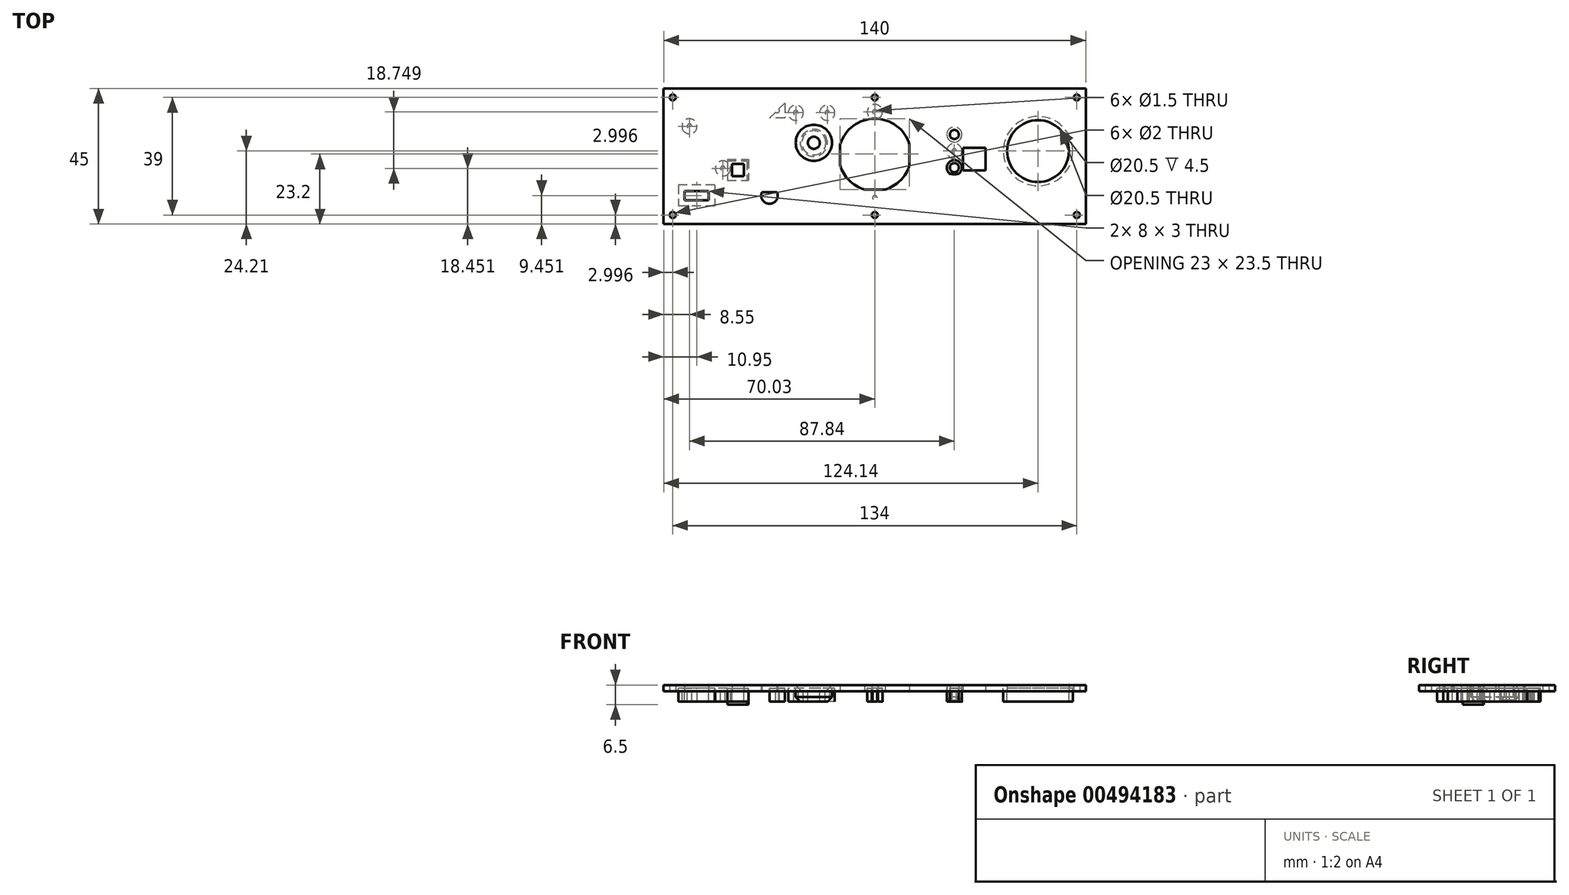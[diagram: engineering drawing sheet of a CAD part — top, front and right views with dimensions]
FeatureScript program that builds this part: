
annotation { "Feature Type Name" : "Feature", "Feature Type Description" : "" }
export const myFeature = defineFeature(function(context is Context, id is Id, definition is map)
    precondition{}
    {
        {
            var Q0;
            Q0=qCreatedBy(makeId("Top.planeOp"),FACE);
            var sketch = newSketch(context, id + "F0", { "sketchPlane" : qUnion([Q0])});
            skLineSegment(sketch, "E0.bottom", {"start": v(12.5, 16.5) * mm, "end": v(1.09, 16.5) * mm});
            skLineSegment(sketch, "E0.top", {"start": v(12.5, -16.5) * mm, "end": v(1.09, -16.5) * mm});
            skLineSegment(sketch, "E0.left", {"start": v(12.5, 16.5) * mm, "end": v(12.5, -16.5) * mm});
            skLineSegment(sketch, "E0.right", {"start": v(-12.5, 16.5) * mm, "end": v(-12.5, -16.5) * mm});
            skPoint(sketch, "E0.middle", {"position": v(0, 0) * mm});
            skCircle(sketch, "E1", {"center": v(0, 0) * mm, "radius": 12 * mm});
            skCircle(sketch, "E2", {"center": v(0, 14.25) * mm, "radius": 0.75 * mm});
            skPoint(sketch, "E2.centerSnap0", {"position": v(0, 16.5) * mm});
            skCircle(sketch, "E3.MirrorC", {"center": v(0, -14.25) * mm, "radius": 0.75 * mm});
            skLineSegment(sketch, "E4.0", {"start": v(9.5, 4.98) * mm, "end": v(9.5, -5.67) * mm, "construction": true});
            skLineSegment(sketch, "E5.bottom", {"start": v(10.77, 1.27) * mm, "end": v(8.23, 1.27) * mm});
            skLineSegment(sketch, "E5.top", {"start": v(10.77, -1.27) * mm, "end": v(8.23, -1.27) * mm});
            skLineSegment(sketch, "E5.left", {"start": v(10.77, 1.27) * mm, "end": v(10.77, -1.27) * mm});
            skLineSegment(sketch, "E5.right", {"start": v(8.23, 1.27) * mm, "end": v(8.23, -1.27) * mm});
            skPoint(sketch, "E5.middle", {"position": v(9.5, 0) * mm});
            skPoint(sketch, "E5.middle.positionSnap0", {"position": v(12.5, 0) * mm});
            skPoint(sketch, "E5.centerSnap0", {"position": v(12.5, 0) * mm});
            skLineSegment(sketch, "E6.MirrorCS", {"start": v(8.23, 1.27) * mm, "end": v(8.23, 3.81) * mm});
            skLineSegment(sketch, "E7.MirrorCS", {"start": v(10.77, 1.27) * mm, "end": v(10.77, 3.81) * mm});
            skLineSegment(sketch, "E8.MirrorCS", {"start": v(10.77, 3.81) * mm, "end": v(8.23, 3.81) * mm});
            skPoint(sketch, "E9.MirrorP", {"position": v(9.5, 2.54) * mm});
            skLineSegment(sketch, "E10.MirrorCS", {"start": v(8.23, -3.81) * mm, "end": v(8.23, -1.27) * mm});
            skLineSegment(sketch, "E11.MirrorCS", {"start": v(10.77, -3.8) * mm, "end": v(10.77, -1.27) * mm});
            skLineSegment(sketch, "E12.MirrorCS", {"start": v(10.77, -3.8) * mm, "end": v(8.23, -3.81) * mm});
            skPoint(sketch, "E13.MirrorP", {"position": v(9.5, -2.54) * mm});
            skLineSegment(sketch, "E14.bottom", {"start": v(-11.5, 11.5) * mm, "end": v(11.5, 11.5) * mm});
            skLineSegment(sketch, "E14.top", {"start": v(-11.5, -11.5) * mm, "end": v(11.5, -11.5) * mm});
            skLineSegment(sketch, "E14.left", {"start": v(-11.5, 11.5) * mm, "end": v(-11.5, -11.5) * mm});
            skLineSegment(sketch, "E14.right", {"start": v(11.5, 11.5) * mm, "end": v(11.5, -11.5) * mm});
            skArc(sketch, "E15", {"start": v(1, 11.96) * mm, "mid": v(0, 16.75) * mm, "end": v(-1, 11.96) * mm});
            skArc(sketch, "E16.MirrorC", {"start": v(1, -11.96) * mm, "mid": v(0, -16.75) * mm, "end": v(-1, -11.96) * mm});
            skLineSegment(sketch, "E17.trimOffspring", {"start": v(-1.09, -16.5) * mm, "end": v(-12.5, -16.5) * mm});
            skLineSegment(sketch, "E18.trimOffspring", {"start": v(-1.09, 16.5) * mm, "end": v(-12.5, 16.5) * mm});
            skSolve(sketch);
        }
        {
            var Q0;
            Q0=qCreatedBy(makeId("Top.planeOp"),FACE);
            var sketch = newSketch(context, id + "F1", { "sketchPlane" : qUnion([Q0])});
            skPoint(sketch, "E19.middle", {"position": v(39.17, 0) * mm});
            skLineSegment(sketch, "E20.bottom", {"start": v(20.93, 1.26) * mm, "end": v(18.4, 1.26) * mm});
            skLineSegment(sketch, "E20.top", {"start": v(20.93, -1.28) * mm, "end": v(18.4, -1.28) * mm});
            skLineSegment(sketch, "E20.left", {"start": v(20.93, 1.26) * mm, "end": v(20.93, -1.28) * mm});
            skLineSegment(sketch, "E20.right", {"start": v(18.4, 1.26) * mm, "end": v(18.4, -1.28) * mm});
            skPoint(sketch, "E20.middle", {"position": v(19.66, 0) * mm});
            skLineSegment(sketch, "E21.MirrorCS", {"start": v(18.4, 1.26) * mm, "end": v(18.4, 3.8) * mm});
            skLineSegment(sketch, "E22.MirrorCS", {"start": v(20.93, 1.26) * mm, "end": v(20.93, 3.8) * mm});
            skLineSegment(sketch, "E23.MirrorCS", {"start": v(20.93, 3.8) * mm, "end": v(18.4, 3.8) * mm});
            skPoint(sketch, "E24.MirrorP", {"position": v(19.66, 2.53) * mm});
            skLineSegment(sketch, "E25.MirrorCS", {"start": v(18.4, -3.82) * mm, "end": v(18.4, -1.28) * mm});
            skLineSegment(sketch, "E26.MirrorCS", {"start": v(20.93, -3.82) * mm, "end": v(20.93, -1.28) * mm});
            skLineSegment(sketch, "E27.MirrorCS", {"start": v(20.93, -3.82) * mm, "end": v(18.4, -3.82) * mm});
            skPoint(sketch, "E28.MirrorP", {"position": v(19.66, -2.55) * mm});
            skLineSegment(sketch, "E29", {"start": v(13.21, 0) * mm, "end": v(-19.23, 0) * mm, "construction": true});
            skLineSegment(sketch, "E30.MirrorCS", {"start": v(18.39, 6.34) * mm, "end": v(18.39, 3.8) * mm});
            skLineSegment(sketch, "E31.MirrorCS", {"start": v(20.93, 6.34) * mm, "end": v(20.93, 3.8) * mm});
            skLineSegment(sketch, "E32.MirrorCS", {"start": v(20.93, 6.34) * mm, "end": v(18.4, 6.34) * mm});
            skPoint(sketch, "E33", {"position": v(64.36, 0) * mm});
            skLineSegment(sketch, "E34", {"start": v(13.1, 1.26) * mm, "end": v(69, 1.26) * mm, "construction": true});
            skCircle(sketch, "E35", {"center": v(54.1, 1.26) * mm, "radius": 10.25 * mm});
            skLineSegment(sketch, "E36.top", {"start": v(47.12, -6.24) * mm, "end": v(14.16, -6.24) * mm});
            skLineSegment(sketch, "E36.right", {"start": v(14.16, 8.76) * mm, "end": v(14.16, -6.24) * mm});
            skPoint(sketch, "E36.middle", {"position": v(39.16, 1.26) * mm});
            skLineSegment(sketch, "E37.trimOffspring", {"start": v(47.12, 8.76) * mm, "end": v(14.16, 8.76) * mm});
            skPoint(sketch, "E38.orphan", {"position": v(64.16, 8.76) * mm});
            skPoint(sketch, "E39.orphan", {"position": v(64.16, -6.24) * mm});
            skLineSegment(sketch, "E40.0", {"start": v(19.66, 8.58) * mm, "end": v(19.66, -6.42) * mm, "construction": true});
            skPoint(sketch, "E41.MirrorP", {"position": v(19.66, 3.79) * mm});
            skPoint(sketch, "E42.MirrorP", {"position": v(19.66, -1.3) * mm});
            skPoint(sketch, "E43.MirrorP", {"position": v(19.66, -3.83) * mm});
            skPoint(sketch, "E44", {"position": v(64.36, 1.26) * mm});
            skLineSegment(sketch, "E45.0", {"start": v(26.36, 7.81) * mm, "end": v(26.36, -5.3) * mm, "construction": true});
            skCircle(sketch, "E46", {"center": v(26.36, 1.26) * mm, "radius": 1.25 * mm});
            skCircle(sketch, "E47", {"center": v(26.36, 6.76) * mm, "radius": 1.5 * mm});
            skCircle(sketch, "E48.MirrorC", {"center": v(26.36, -4.24) * mm, "radius": 1.5 * mm});
            skLineSegment(sketch, "E49.bottom", {"start": v(29.26, 2.36) * mm, "end": v(36.76, 2.36) * mm});
            skLineSegment(sketch, "E49.top", {"start": v(29.26, -5.14) * mm, "end": v(36.76, -5.14) * mm});
            skLineSegment(sketch, "E49.left", {"start": v(29.26, 2.36) * mm, "end": v(29.26, -5.14) * mm});
            skLineSegment(sketch, "E49.right", {"start": v(36.76, 2.36) * mm, "end": v(36.76, -5.14) * mm});
            skCircle(sketch, "E50", {"center": v(26.36, -4.24) * mm, "radius": 2.5 * mm});
            skCircle(sketch, "E51.MirrorC", {"center": v(26.36, 6.76) * mm, "radius": 2.5 * mm});
            skCircle(sketch, "E52", {"center": v(26.36, 1.26) * mm, "radius": 0.75 * mm});
            skCircle(sketch, "E53", {"center": v(26.36, 1.26) * mm, "radius": 2.5 * mm});
            skCircle(sketch, "E54", {"center": v(54.1, 1.26) * mm, "radius": 11.5 * mm});
            skLineSegment(sketch, "E55", {"start": v(39.17, 0) * mm, "end": v(39.17, 13.48) * mm, "construction": true});
            skPoint(sketch, "E56", {"position": v(39.17, 1.26) * mm});
            skSolve(sketch);
        }
        {
            var Q0;
            Q0=qCreatedBy(makeId("Top.planeOp"),FACE);
            var sketch = newSketch(context, id + "F2", { "sketchPlane" : qUnion([Q0])});
            skLineSegment(sketch, "E57.bottom", {"start": v(-13.23, 16.5) * mm, "end": v(-28.73, 16.5) * mm});
            skLineSegment(sketch, "E57.top", {"start": v(-13.23, -16.5) * mm, "end": v(-28.73, -16.5) * mm});
            skLineSegment(sketch, "E57.left", {"start": v(-13.23, 16.5) * mm, "end": v(-13.23, -16.5) * mm});
            skLineSegment(sketch, "E57.right", {"start": v(-28.73, 16.5) * mm, "end": v(-28.73, -16.5) * mm});
            skPoint(sketch, "E57.middle", {"position": v(-20.98, 0) * mm});
            skLineSegment(sketch, "E58.0", {"start": v(-12.04, -13.5) * mm, "end": v(-29.92, -13.5) * mm, "construction": true});
            skLineSegment(sketch, "E59.bottom", {"start": v(-19.7, -11.73) * mm, "end": v(-22.25, -11.73) * mm});
            skLineSegment(sketch, "E59.top", {"start": v(-19.7, -15.27) * mm, "end": v(-22.25, -15.27) * mm});
            skLineSegment(sketch, "E59.left", {"start": v(-19.7, -11.73) * mm, "end": v(-19.7, -15.27) * mm});
            skLineSegment(sketch, "E59.right", {"start": v(-22.25, -11.73) * mm, "end": v(-22.25, -15.27) * mm});
            skPoint(sketch, "E59.middle", {"position": v(-20.98, -13.5) * mm});
            skLineSegment(sketch, "E60.MirrorCS", {"start": v(-19.7, -11.73) * mm, "end": v(-17.17, -11.73) * mm});
            skLineSegment(sketch, "E61.MirrorCS", {"start": v(-17.17, -11.73) * mm, "end": v(-17.17, -15.27) * mm});
            skLineSegment(sketch, "E62.MirrorCS", {"start": v(-19.7, -15.27) * mm, "end": v(-17.17, -15.27) * mm});
            skPoint(sketch, "E63.MirrorP", {"position": v(-18.44, -13.5) * mm});
            skLineSegment(sketch, "E64.MirrorCS", {"start": v(-14.63, -11.73) * mm, "end": v(-17.17, -11.73) * mm});
            skLineSegment(sketch, "E65.MirrorCS", {"start": v(-14.63, -11.73) * mm, "end": v(-14.63, -15.27) * mm});
            skLineSegment(sketch, "E66.MirrorCS", {"start": v(-14.63, -15.27) * mm, "end": v(-17.17, -15.27) * mm});
            skPoint(sketch, "E67.MirrorP", {"position": v(-15.9, -13.5) * mm});
            skLineSegment(sketch, "E68.MirrorCS", {"start": v(-24.79, -11.73) * mm, "end": v(-24.79, -15.27) * mm});
            skLineSegment(sketch, "E69.MirrorCS", {"start": v(-24.79, -11.73) * mm, "end": v(-22.25, -11.73) * mm});
            skLineSegment(sketch, "E70.MirrorCS", {"start": v(-24.79, -15.27) * mm, "end": v(-22.25, -15.27) * mm});
            skPoint(sketch, "E71.MirrorP", {"position": v(-23.52, -13.5) * mm});
            skPoint(sketch, "E72.MirrorP", {"position": v(-26.06, -13.5) * mm});
            skLineSegment(sketch, "E73.MirrorCS", {"start": v(-24.79, -11.73) * mm, "end": v(-27.33, -11.73) * mm});
            skLineSegment(sketch, "E74.MirrorCS", {"start": v(-27.33, -11.73) * mm, "end": v(-27.33, -15.27) * mm});
            skLineSegment(sketch, "E75.MirrorCS", {"start": v(-24.79, -15.27) * mm, "end": v(-27.33, -15.27) * mm});
            skLineSegment(sketch, "E76", {"start": v(-20.98, 19.3) * mm, "end": v(-20.98, -17.5) * mm, "construction": true});
            skPoint(sketch, "E76.startSnap0", {"position": v(-20.98, 16.5) * mm});
            skCircle(sketch, "E77", {"center": v(-26.2, 13.96) * mm, "radius": 1.25 * mm});
            skCircle(sketch, "E78.MirrorC", {"center": v(-15.77, 13.96) * mm, "radius": 1.25 * mm});
            skLineSegment(sketch, "E79.bottom", {"start": v(-19.48, 5.25) * mm, "end": v(-20.98, 5.25) * mm});
            skLineSegment(sketch, "E79.top", {"start": v(-19.48, 2.75) * mm, "end": v(-20.98, 2.75) * mm});
            skLineSegment(sketch, "E79.left", {"start": v(-19.48, 5.25) * mm, "end": v(-19.48, 2.75) * mm});
            skLineSegment(sketch, "E79.right", {"start": v(-20.98, 5.25) * mm, "end": v(-20.98, 2.75) * mm});
            skPoint(sketch, "E79.middle", {"position": v(-20.23, 4) * mm});
            skCircle(sketch, "E80", {"center": v(-20.23, 4) * mm, "radius": 2 * mm});
            skCircle(sketch, "E81", {"center": v(-20.23, 4) * mm, "radius": 6 * mm});
            skCircle(sketch, "E82", {"center": v(-26.2, 13.96) * mm, "radius": 2.5 * mm});
            skCircle(sketch, "E83.MirrorC", {"center": v(-15.77, 13.96) * mm, "radius": 2.5 * mm});
            skCircle(sketch, "E84", {"center": v(-26.2, 13.96) * mm, "radius": 0.75 * mm});
            skCircle(sketch, "E85.MirrorC", {"center": v(-15.77, 13.96) * mm, "radius": 0.75 * mm});
            skSolve(sketch);
        }
        {
            var Q0;
            Q0=qCreatedBy(makeId("Top.planeOp"),FACE);
            var sketch = newSketch(context, id + "F3", { "sketchPlane" : qUnion([Q0])});
            skLineSegment(sketch, "E86.bottom", {"start": v(-70.03, 22.05) * mm, "end": v(69.97, 22.05) * mm});
            skLineSegment(sketch, "E86.top", {"start": v(-70.03, -22.95) * mm, "end": v(69.97, -22.95) * mm});
            skLineSegment(sketch, "E86.left", {"start": v(-70.03, 22.05) * mm, "end": v(-70.03, -22.95) * mm});
            skLineSegment(sketch, "E86.right", {"start": v(69.97, 22.05) * mm, "end": v(69.97, -22.95) * mm});
            skCircle(sketch, "E87", {"center": v(-67.03, 19.05) * mm, "radius": 1 * mm});
            skCircle(sketch, "E88", {"center": v(-67.03, -19.95) * mm, "radius": 1 * mm});
            skCircle(sketch, "E89", {"center": v(66.97, 19.05) * mm, "radius": 1 * mm});
            skCircle(sketch, "E90", {"center": v(66.97, -19.95) * mm, "radius": 1 * mm});
            skCircle(sketch, "E91", {"center": v(-0.03, 19.05) * mm, "radius": 1 * mm});
            skPoint(sketch, "E91.centerSnap0", {"position": v(-0.03, 22.05) * mm});
            skCircle(sketch, "E92", {"center": v(-0.03, -19.95) * mm, "radius": 1 * mm});
            skPoint(sketch, "E92.centerSnap0", {"position": v(-0.03, -22.95) * mm});
            skSolve(sketch);
        }
        {
            var Q0;
            Q0=qCreatedBy(makeId("Top.planeOp"),FACE);
            var sketch = newSketch(context, id + "F4", { "sketchPlane" : qUnion([Q0])});
            skCircle(sketch, "E93", {"center": v(-34.95, -13.5) * mm, "radius": 2.75 * mm});
            skLineSegment(sketch, "E94.bottom", {"start": v(-52.9, -15) * mm, "end": v(-42.4, -15) * mm});
            skLineSegment(sketch, "E94.top", {"start": v(-52.9, -2) * mm, "end": v(-42.4, -2) * mm});
            skLineSegment(sketch, "E94.left", {"start": v(-52.9, -15) * mm, "end": v(-52.9, -2) * mm});
            skLineSegment(sketch, "E94.right", {"start": v(-42.4, -15) * mm, "end": v(-42.4, -2) * mm});
            skLineSegment(sketch, "E95", {"start": v(-63.63, -13.5) * mm, "end": v(-29.18, -13.5) * mm, "construction": true});
            skPoint(sketch, "E96", {"position": v(-47.65, -15) * mm});
            skLineSegment(sketch, "E97.bottom", {"start": v(-47.4, -3) * mm, "end": v(-43.4, -3) * mm});
            skLineSegment(sketch, "E97.top", {"start": v(-47.4, -7) * mm, "end": v(-43.4, -7) * mm});
            skLineSegment(sketch, "E97.left", {"start": v(-47.4, -3) * mm, "end": v(-47.4, -7) * mm});
            skLineSegment(sketch, "E97.right", {"start": v(-43.4, -3) * mm, "end": v(-43.4, -7) * mm});
            skLineSegment(sketch, "E98", {"start": v(-32.41, -12.35) * mm, "end": v(-32.41, -14.67) * mm});
            skPoint(sketch, "E99", {"position": v(-31.14, -13.5) * mm});
            skLineSegment(sketch, "E100.0", {"start": v(-34.95, -12.35) * mm, "end": v(-34.95, -14.67) * mm});
            skLineSegment(sketch, "E101.0", {"start": v(-37.5, -12.35) * mm, "end": v(-37.5, -14.67) * mm});
            skLineSegment(sketch, "E102.0", {"start": v(-40.03, -12.35) * mm, "end": v(-40.03, -14.67) * mm});
            skLineSegment(sketch, "E103.0", {"start": v(-29.87, -12.35) * mm, "end": v(-29.87, -14.67) * mm});
            skPoint(sketch, "E104.MirrorP", {"position": v(-33.68, -13.5) * mm});
            skPoint(sketch, "E105.MirrorP", {"position": v(-36.22, -13.5) * mm});
            skPoint(sketch, "E106.MirrorP", {"position": v(-38.76, -13.5) * mm});
            skLineSegment(sketch, "E107.MirrorCS", {"start": v(-42.57, -12.35) * mm, "end": v(-42.57, -14.67) * mm});
            skLineSegment(sketch, "E108.MirrorCS", {"start": v(-47.65, -12.85) * mm, "end": v(-47.65, -14.67) * mm});
            skLineSegment(sketch, "E109.MirrorCS", {"start": v(-50.2, -12.35) * mm, "end": v(-50.2, -14.67) * mm});
            skPoint(sketch, "E110.MirrorP", {"position": v(-43.84, -13.5) * mm});
            skPoint(sketch, "E111.MirrorP", {"position": v(-46.38, -13.5) * mm});
            skLineSegment(sketch, "E112.trimOffspring", {"start": v(-40.03, -12.35) * mm, "end": v(-29.87, -12.35) * mm});
            skLineSegment(sketch, "E113.trimOffspring", {"start": v(-40.03, -14.67) * mm, "end": v(-29.87, -14.67) * mm});
            skLineSegment(sketch, "E114.MirrorCS", {"start": v(-52.73, -12.35) * mm, "end": v(-52.73, -14.67) * mm});
            skPoint(sketch, "E115.MirrorP", {"position": v(-48.92, -13.5) * mm});
            skPoint(sketch, "E116.MirrorP", {"position": v(-51.46, -14) * mm});
            skPoint(sketch, "E117.MirrorP", {"position": v(-59.08, -13.5) * mm});
            skLineSegment(sketch, "E118.trimOffspring", {"start": v(-52.73, -14.67) * mm, "end": v(-42.57, -14.67) * mm});
            skLineSegment(sketch, "E119.trimOffspring", {"start": v(-52.73, -12.35) * mm, "end": v(-42.57, -12.35) * mm});
            skCircle(sketch, "E120", {"center": v(-50.4, -4.5) * mm, "radius": 1.5 * mm});
            skCircle(sketch, "E121", {"center": v(-50.4, -4.5) * mm, "radius": 2.5 * mm});
            skCircle(sketch, "E122", {"center": v(-50.4, -4.5) * mm, "radius": 0.75 * mm});
            skLineSegment(sketch, "E123.bottom", {"start": v(-55.08, -12) * mm, "end": v(-63.08, -12) * mm});
            skLineSegment(sketch, "E123.top", {"start": v(-55.08, -15) * mm, "end": v(-63.08, -15) * mm});
            skLineSegment(sketch, "E123.left", {"start": v(-55.08, -12) * mm, "end": v(-55.08, -15) * mm});
            skLineSegment(sketch, "E123.right", {"start": v(-63.08, -12) * mm, "end": v(-63.08, -15) * mm});
            skLineSegment(sketch, "E124.0", {"start": v(-53.08, -10) * mm, "end": v(-65.08, -10) * mm});
            skLineSegment(sketch, "E124.1", {"start": v(-53.08, -10) * mm, "end": v(-53.08, -17) * mm});
            skLineSegment(sketch, "E124.2", {"start": v(-53.08, -17) * mm, "end": v(-65.08, -17) * mm});
            skLineSegment(sketch, "E124.3", {"start": v(-65.08, -10) * mm, "end": v(-65.08, -17) * mm});
            skLineSegment(sketch, "E125.MirrorCS", {"start": v(-45.11, -12.35) * mm, "end": v(-45.11, -14.67) * mm});
            skLineSegment(sketch, "E126", {"start": v(-33.68, -13.5) * mm, "end": v(-33.68, 11.55) * mm, "construction": true});
            skLineSegment(sketch, "E127.0", {"start": v(-48.9, -1.5) * mm, "end": v(-41.9, -1.5) * mm});
            skLineSegment(sketch, "E127.1", {"start": v(-48.9, -1.5) * mm, "end": v(-48.9, -8.5) * mm});
            skLineSegment(sketch, "E127.2", {"start": v(-48.9, -8.5) * mm, "end": v(-41.9, -8.5) * mm});
            skLineSegment(sketch, "E127.3", {"start": v(-41.9, -1.5) * mm, "end": v(-41.9, -8.5) * mm});
            skSolve(sketch);
        }
        {
            var Q0;
            Q0=qCreatedBy(makeId("Top.planeOp"),FACE);
            var sketch = newSketch(context, id + "F5", { "sketchPlane" : qUnion([Q0])});
            skLineSegment(sketch, "E128.bottom", {"start": v(-32.4, 10.5) * mm, "end": v(-34.95, 10.5) * mm});
            skLineSegment(sketch, "E128.top", {"start": v(-32.4, 7.97) * mm, "end": v(-34.95, 7.97) * mm});
            skLineSegment(sketch, "E128.left", {"start": v(-32.4, 10.5) * mm, "end": v(-32.4, 7.97) * mm});
            skLineSegment(sketch, "E128.right", {"start": v(-34.95, 10.5) * mm, "end": v(-34.95, 7.97) * mm});
            skPoint(sketch, "E128.middle", {"position": v(-33.68, 9.24) * mm});
            skLineSegment(sketch, "E129.MirrorCS", {"start": v(-34.95, 5.55) * mm, "end": v(-34.95, 8.1) * mm});
            skLineSegment(sketch, "E130.MirrorCS", {"start": v(-32.4, 5.55) * mm, "end": v(-34.95, 5.55) * mm});
            skLineSegment(sketch, "E131.MirrorCS", {"start": v(-32.41, 5.55) * mm, "end": v(-32.41, 8.1) * mm});
            skPoint(sketch, "E132.MirrorP", {"position": v(-33.68, 6.82) * mm});
            skLineSegment(sketch, "E133.MirrorCS", {"start": v(-32.4, 3) * mm, "end": v(-34.95, 3) * mm});
            skLineSegment(sketch, "E134.MirrorCS", {"start": v(-34.95, 5.55) * mm, "end": v(-34.95, 3) * mm});
            skLineSegment(sketch, "E135.MirrorCS", {"start": v(-32.41, 5.55) * mm, "end": v(-32.41, 3) * mm});
            skPoint(sketch, "E136.MirrorP", {"position": v(-33.68, 4.28) * mm});
            skLineSegment(sketch, "E137.bottom", {"start": v(-63.88, 17.24) * mm, "end": v(-29.88, 17.24) * mm});
            skLineSegment(sketch, "E137.top", {"start": v(-63.88, 1.74) * mm, "end": v(-40.48, 1.74) * mm});
            skLineSegment(sketch, "E137.left", {"start": v(-63.88, 17.24) * mm, "end": v(-63.88, 1.74) * mm});
            skLineSegment(sketch, "E137.right", {"start": v(-29.88, 17.24) * mm, "end": v(-29.88, -1.18) * mm});
            skLineSegment(sketch, "E138.MirrorCS", {"start": v(-32.4, 0.47) * mm, "end": v(-34.95, 0.47) * mm});
            skLineSegment(sketch, "E139.MirrorCS", {"start": v(-34.95, 0.47) * mm, "end": v(-34.95, 3) * mm});
            skLineSegment(sketch, "E140.MirrorCS", {"start": v(-32.41, 0.47) * mm, "end": v(-32.41, 3) * mm});
            skPoint(sketch, "E141.MirrorP", {"position": v(-33.68, 1.74) * mm});
            skLineSegment(sketch, "E142.top", {"start": v(-29.88, -1.18) * mm, "end": v(-36.88, -1.18) * mm});
            skLineSegment(sketch, "E143", {"start": v(-36.88, -1.18) * mm, "end": v(-40.48, 1.74) * mm});
            skCircle(sketch, "E144", {"center": v(-61.48, 9.5) * mm, "radius": 1.5 * mm});
            skPoint(sketch, "E144.centerSnap0", {"position": v(-63.88, 9.5) * mm});
            skLineSegment(sketch, "E145.bottom", {"start": v(-58.88, 17.24) * mm, "end": v(-38.38, 17.24) * mm});
            skLineSegment(sketch, "E145.top", {"start": v(-58.88, 1.74) * mm, "end": v(-38.38, 1.74) * mm});
            skLineSegment(sketch, "E145.left", {"start": v(-58.88, 17.24) * mm, "end": v(-58.88, 1.74) * mm});
            skLineSegment(sketch, "E145.right", {"start": v(-38.38, 17.24) * mm, "end": v(-38.38, 1.74) * mm});
            skPoint(sketch, "E145.middle", {"position": v(-48.63, 9.5) * mm});
            skLineSegment(sketch, "E146.bottom", {"start": v(-58.88, 17.24) * mm, "end": v(-61.38, 17.24) * mm});
            skLineSegment(sketch, "E146.top", {"start": v(-58.88, 1.74) * mm, "end": v(-61.38, 1.74) * mm});
            skLineSegment(sketch, "E146.right", {"start": v(-63.88, 14.74) * mm, "end": v(-63.88, 4.24) * mm});
            skPoint(sketch, "E147.visualSharp", {"position": v(-63.88, 17.24) * mm});
            skArc(sketch, "E147.filletArc", {"start": v(-61.38, 17.24) * mm, "mid": v(-63.15, 16.5) * mm, "end": v(-63.88, 14.74) * mm});
            skPoint(sketch, "E148.visualSharp", {"position": v(-63.88, 1.74) * mm});
            skArc(sketch, "E148.filletArc", {"start": v(-63.88, 4.24) * mm, "mid": v(-63.15, 2.47) * mm, "end": v(-61.38, 1.74) * mm});
            skCircle(sketch, "E149", {"center": v(-61.48, 9.5) * mm, "radius": 0.75 * mm});
            skCircle(sketch, "E150", {"center": v(-61.48, 9.5) * mm, "radius": 2.5 * mm});
            skLineSegment(sketch, "E151.bottom", {"start": v(-29.88, 17.24) * mm, "end": v(-34.88, 17.24) * mm});
            skLineSegment(sketch, "E151.top", {"start": v(-29.88, 12.24) * mm, "end": v(-34.88, 12.24) * mm});
            skLineSegment(sketch, "E151.left", {"start": v(-29.88, 17.24) * mm, "end": v(-29.88, 12.24) * mm});
            skLineSegment(sketch, "E151.right", {"start": v(-34.88, 17.24) * mm, "end": v(-34.88, 12.24) * mm});
            skLineSegment(sketch, "E152", {"start": v(-34.88, 12.24) * mm, "end": v(-29.88, 17.24) * mm});
            skCircle(sketch, "E153", {"center": v(-32.38, 14.74) * mm, "radius": 0.75 * mm});
            skSolve(sketch);
        }
        {
            var Q0;
            Q0=makeQuery(id+"F3.imprint","IMPRINT",FACE,{"disambiguationData":[TD([[makeQuery(id+"F3.imprint","IMPRINT",EDGE,{"derivedFrom":sQuery(id+"F3.wireOp",EDGE,"E86.bottom")}),-1.0]])]});
            extrude(context, id + "F6", {"entities" : qUnion([Q0]), "endBound" : BoundingType.SYMMETRIC, "depth" : 2 * mm, "offsetDistance" : 25 * mm});
        }
        {
            var Q0;
            Q0=makeQuery(id+"F5.imprint","IMPRINT",FACE,{"disambiguationData":[TD([[makeQuery(id+"F5.imprint","IMPRINT",EDGE,{"derivedFrom":sQuery(id+"F5.wireOp",EDGE,"E151.bottom")}),1.0]])]});
            var Q1;
            Q1=makeQuery(id+"F2.imprint","IMPRINT",FACE,{"disambiguationData":[TD([[makeQuery(id+"F2.imprint","IMPRINT",EDGE,{"derivedFrom":sQuery(id+"F2.wireOp",EDGE,"E77")}),1.0]])]});
            var Q2;
            Q2=makeQuery(id+"F2.imprint","IMPRINT",FACE,{"disambiguationData":[TD([[makeQuery(id+"F2.imprint","IMPRINT",EDGE,{"derivedFrom":sQuery(id+"F2.wireOp",EDGE,"E77")}),-1.0]])]});
            var Q3;
            Q3=makeQuery(id+"F2.imprint","IMPRINT",FACE,{"disambiguationData":[TD([[makeQuery(id+"F2.imprint","IMPRINT",EDGE,{"derivedFrom":sQuery(id+"F2.wireOp",EDGE,"E78.MirrorC")}),-1.0]])]});
            var Q4;
            Q4=makeQuery(id+"F2.imprint","IMPRINT",FACE,{"disambiguationData":[TD([[makeQuery(id+"F2.imprint","IMPRINT",EDGE,{"derivedFrom":sQuery(id+"F2.wireOp",EDGE,"E78.MirrorC")}),1.0]])]});
            var Q5;
            Q5=makeQuery(id+"F2.imprint","IMPRINT",FACE,{"disambiguationData":[TD([[makeQuery(id+"F2.imprint","IMPRINT",EDGE,{"derivedFrom":sQuery(id+"F2.wireOp",EDGE,"E80")}),-1.0]])]});
            var Q6;
            Q6=makeQuery(id+"F4.imprint","IMPRINT",FACE,{"disambiguationData":[TD([[makeQuery(id+"F4.imprint","IMPRINT",EDGE,{"derivedFrom":sQuery(id+"F4.wireOp",EDGE,"E123.bottom")}),-1.0]])]});
            var Q7;
            Q7=makeQuery(id+"F4.imprint","IMPRINT",FACE,{"disambiguationData":[TD([[makeQuery(id+"F4.imprint","IMPRINT",EDGE,{"derivedFrom":sQuery(id+"F4.wireOp",EDGE,"E120")}),1.0]])]});
            var Q8;
            Q8=makeQuery(id+"F4.imprint","IMPRINT",FACE,{"disambiguationData":[TD([[makeQuery(id+"F4.imprint","IMPRINT",EDGE,{"derivedFrom":sQuery(id+"F4.wireOp",EDGE,"E120")}),-1.0]])]});
            var Q9;
            Q9=makeQuery(id+"F0.imprint","IMPRINT",FACE,{"disambiguationData":[TD([[makeQuery(id+"F0.imprint","IMPRINT",EDGE,{"derivedFrom":sQuery(id+"F0.wireOp",EDGE,"E2")}),-1.0]])]});
            var Q10;
            Q10=makeQuery(id+"F0.imprint","IMPRINT",FACE,{"disambiguationData":[TD([[makeQuery(id+"F0.imprint","IMPRINT",EDGE,{"derivedFrom":sQuery(id+"F0.wireOp",EDGE,"E3.MirrorC")}),1.0]])]});
            var Q11;
            {var subQ0=sQuery(id+"F1.wireOp",EDGE,"E51.MirrorC");var subQ1=sQuery(id+"F1.wireOp",EDGE,"E37.trimOffspring");var subQ2=makeQuery(id+"F1.imprint","INTERSECT",VERTEX,{"disambiguationData":[OD(0.0)],"derivedFrom":[subQ1,subQ0]});Q11=makeQuery(id+"F1.imprint","IMPRINT",FACE,{"disambiguationData":[TD([[makeQuery(id+"F1.imprint","IMPRINT",EDGE,{"disambiguationData":[TD([[subQ2,-1.0]])],"derivedFrom":subQ1}),-1.0]])]});}
            var Q12;
            Q12=makeQuery(id+"F1.imprint","IMPRINT",FACE,{"disambiguationData":[TD([[makeQuery(id+"F1.imprint","IMPRINT",EDGE,{"derivedFrom":sQuery(id+"F1.wireOp",EDGE,"E47")}),-1.0]])]});
            var Q13;
            Q13=makeQuery(id+"F1.imprint","IMPRINT",FACE,{"disambiguationData":[TD([[makeQuery(id+"F1.imprint","IMPRINT",EDGE,{"derivedFrom":sQuery(id+"F1.wireOp",EDGE,"E46")}),-1.0]])]});
            var Q14;
            Q14=makeQuery(id+"F1.imprint","IMPRINT",FACE,{"disambiguationData":[TD([[makeQuery(id+"F1.imprint","IMPRINT",EDGE,{"derivedFrom":sQuery(id+"F1.wireOp",EDGE,"E46")}),1.0]])]});
            var Q15;
            Q15=makeQuery(id+"F1.imprint","IMPRINT",FACE,{"disambiguationData":[TD([[makeQuery(id+"F1.imprint","IMPRINT",EDGE,{"derivedFrom":sQuery(id+"F1.wireOp",EDGE,"E48.MirrorC")}),1.0]])]});
            var Q16;
            {var subQ0=sQuery(id+"F1.wireOp",EDGE,"E50");var subQ1=sQuery(id+"F1.wireOp",EDGE,"E36.top");var subQ2=makeQuery(id+"F1.imprint","INTERSECT",VERTEX,{"disambiguationData":[OD(0.0)],"derivedFrom":[subQ1,subQ0]});Q16=makeQuery(id+"F1.imprint","IMPRINT",FACE,{"disambiguationData":[TD([[makeQuery(id+"F1.imprint","IMPRINT",EDGE,{"disambiguationData":[TD([[subQ2,-1.0]])],"derivedFrom":subQ1}),1.0]])]});}
            var Q17;
            {var subQ0=sQuery(id+"F1.wireOp",EDGE,"E36.top");var subQ1=sQuery(id+"F1.wireOp",EDGE,"E35");var subQ2=makeQuery(id+"F1.imprint","INTERSECT",VERTEX,{"derivedFrom":[subQ1,subQ0]});Q17=makeQuery(id+"F1.imprint","IMPRINT",FACE,{"disambiguationData":[TD([[makeQuery(id+"F1.imprint","IMPRINT",EDGE,{"disambiguationData":[TD([[subQ2,-1.0]])],"derivedFrom":subQ1}),-1.0]])]});}
            var Q18;
            {var subQ0=sQuery(id+"F1.wireOp",EDGE,"E36.top");var subQ1=sQuery(id+"F1.wireOp",EDGE,"E35");var subQ2=makeQuery(id+"F1.imprint","INTERSECT",VERTEX,{"derivedFrom":[subQ1,subQ0]});Q18=makeQuery(id+"F1.imprint","IMPRINT",FACE,{"disambiguationData":[TD([[makeQuery(id+"F1.imprint","IMPRINT",EDGE,{"disambiguationData":[TD([[subQ2,1.0]])],"derivedFrom":subQ1}),-1.0]])]});}
            var Q19;
            Q19=makeQuery(id+"F5.imprint","IMPRINT",FACE,{"disambiguationData":[TD([[makeQuery(id+"F5.imprint","IMPRINT",EDGE,{"derivedFrom":sQuery(id+"F5.wireOp",EDGE,"E144")}),1.0]])]});
            var Q20;
            Q20=makeQuery(id+"F5.imprint","IMPRINT",FACE,{"disambiguationData":[TD([[makeQuery(id+"F5.imprint","IMPRINT",EDGE,{"derivedFrom":sQuery(id+"F5.wireOp",EDGE,"E144")}),-1.0]])]});
            var Q21;
            {var subQ1=sQuery(id+"F5.wireOp",EDGE,"E151.top");Q21=makeQuery(id+"F5.imprint","IMPRINT",FACE,{"disambiguationData":[TD([[makeQuery(id+"F5.imprint","IMPRINT",EDGE,{"derivedFrom":subQ1}),-1.0]])]});}
            var Q22;
            Q22=makeQuery(id+"F4.imprint","IMPRINT",FACE,{"disambiguationData":[TD([[makeQuery(id+"F4.imprint","IMPRINT",EDGE,{"derivedFrom":sQuery(id+"F4.wireOp",EDGE,"E97.bottom")}),1.0]])]});
            var Q23;
            {var subQ0=sQuery(id+"F4.wireOp",EDGE,"E127.1");var subQ1=sQuery(id+"F4.wireOp",EDGE,"E121");var subQ2=makeQuery(id+"F4.imprint","INTERSECT",VERTEX,{"disambiguationData":[OD(0.0)],"derivedFrom":[subQ1,subQ0]});Q23=makeQuery(id+"F4.imprint","IMPRINT",FACE,{"disambiguationData":[TD([[makeQuery(id+"F4.imprint","IMPRINT",EDGE,{"disambiguationData":[TD([[subQ2,1.0]])],"derivedFrom":subQ1}),1.0]])]});}
            var Q24;
            {var subQ1=sQuery(id+"F4.wireOp",EDGE,"E127.0");Q24=makeQuery(id+"F4.imprint","IMPRINT",FACE,{"disambiguationData":[TD([[makeQuery(id+"F4.imprint","IMPRINT",EDGE,{"derivedFrom":subQ1}),-1.0]])]});}
            extrude(context, id + "F7", {"entities" : qUnion([Q0, Q1, Q2, Q3, Q4, Q5, Q6, Q7, Q8, Q9, Q10, Q11, Q12, Q13, Q14, Q15, Q16, Q17, Q18, Q19, Q20, Q21, Q22, Q23, Q24]), "oppositeDirection" : true, "depth" : 4.5 * mm, "offsetDistance" : 25 * mm});
        }
        {
            var Q0;
            Q0=makeQuery(id+"F5.imprint","IMPRINT",FACE,{"disambiguationData":[TD([[makeQuery(id+"F5.imprint","IMPRINT",EDGE,{"derivedFrom":sQuery(id+"F5.wireOp",EDGE,"E145.bottom")}),-1.0]])]});
            var Q1;
            Q1=makeQuery(id+"F4.imprint","IMPRINT",FACE,{"disambiguationData":[TD([[makeQuery(id+"F4.imprint","IMPRINT",EDGE,{"derivedFrom":sQuery(id+"F4.wireOp",EDGE,"E123.bottom")}),1.0]])]});
            var Q2;
            Q2=makeQuery(id+"F4.imprint","IMPRINT",FACE,{"disambiguationData":[TD([[makeQuery(id+"F4.imprint","IMPRINT",EDGE,{"derivedFrom":sQuery(id+"F4.wireOp",EDGE,"E97.bottom")}),-1.0]])]});
            var Q3;
            {var subQ0=sQuery(id+"F4.wireOp",EDGE,"E98");var subQ1=sQuery(id+"F4.wireOp",EDGE,"E93");var subQ2=makeQuery(id+"F4.imprint","INTERSECT",VERTEX,{"disambiguationData":[OD(0.0)],"derivedFrom":[subQ1,subQ0]});Q3=makeQuery(id+"F4.imprint","IMPRINT",FACE,{"disambiguationData":[TD([[makeQuery(id+"F4.imprint","IMPRINT",EDGE,{"disambiguationData":[TD([[subQ2,1.0]])],"derivedFrom":subQ1}),1.0]])]});}
            var Q4;
            {var subQ0=sQuery(id+"F4.wireOp",EDGE,"E100.0");Q4=makeQuery(id+"F4.imprint","IMPRINT",FACE,{"disambiguationData":[TD([[makeQuery(id+"F4.imprint","IMPRINT",EDGE,{"derivedFrom":subQ0}),1.0]])]});}
            var Q5;
            {var subQ0=sQuery(id+"F4.wireOp",EDGE,"E112.trimOffspring");var subQ1=sQuery(id+"F4.wireOp",EDGE,"E93");var subQ2=makeQuery(id+"F4.imprint","INTERSECT",VERTEX,{"disambiguationData":[OD(0.0)],"derivedFrom":[subQ1,subQ0]});Q5=makeQuery(id+"F4.imprint","IMPRINT",FACE,{"disambiguationData":[TD([[makeQuery(id+"F4.imprint","IMPRINT",EDGE,{"disambiguationData":[TD([[subQ2,1.0]])],"derivedFrom":subQ1}),-1.0]])]});}
            var Q6;
            {var subQ0=sQuery(id+"F4.wireOp",EDGE,"E112.trimOffspring");var subQ1=sQuery(id+"F4.wireOp",EDGE,"E93");var subQ2=makeQuery(id+"F4.imprint","INTERSECT",VERTEX,{"disambiguationData":[OD(0.0)],"derivedFrom":[subQ1,subQ0]});Q6=makeQuery(id+"F4.imprint","IMPRINT",FACE,{"disambiguationData":[TD([[makeQuery(id+"F4.imprint","IMPRINT",EDGE,{"disambiguationData":[TD([[subQ2,-1.0]])],"derivedFrom":subQ1}),1.0]])]});}
            var Q7;
            {var subQ4=sQuery(id+"F4.wireOp",EDGE,"E100.0");Q7=makeQuery(id+"F4.imprint","IMPRINT",FACE,{"disambiguationData":[TD([[makeQuery(id+"F4.imprint","IMPRINT",EDGE,{"derivedFrom":subQ4}),-1.0]])]});}
            var Q8;
            {var subQ0=sQuery(id+"F4.wireOp",EDGE,"E113.trimOffspring");var subQ1=sQuery(id+"F4.wireOp",EDGE,"E93");var subQ2=makeQuery(id+"F4.imprint","INTERSECT",VERTEX,{"disambiguationData":[OD(0.0)],"derivedFrom":[subQ1,subQ0]});Q8=makeQuery(id+"F4.imprint","IMPRINT",FACE,{"disambiguationData":[TD([[makeQuery(id+"F4.imprint","IMPRINT",EDGE,{"disambiguationData":[TD([[subQ2,-1.0]])],"derivedFrom":subQ1}),1.0]])]});}
            var Q9;
            {var subQ0=sQuery(id+"F4.wireOp",EDGE,"E101.0");var subQ1=sQuery(id+"F4.wireOp",EDGE,"E93");var subQ2=makeQuery(id+"F4.imprint","INTERSECT",VERTEX,{"disambiguationData":[OD(0.0)],"derivedFrom":[subQ1,subQ0]});Q9=makeQuery(id+"F4.imprint","IMPRINT",FACE,{"disambiguationData":[TD([[makeQuery(id+"F4.imprint","IMPRINT",EDGE,{"disambiguationData":[TD([[subQ2,-1.0]])],"derivedFrom":subQ1}),1.0]])]});}
            var Q10;
            {var subQ0=sQuery(id+"F4.wireOp",EDGE,"E112.trimOffspring");var subQ1=sQuery(id+"F4.wireOp",EDGE,"E93");var subQ2=makeQuery(id+"F4.imprint","INTERSECT",VERTEX,{"disambiguationData":[OD(1.0)],"derivedFrom":[subQ1,subQ0]});Q10=makeQuery(id+"F4.imprint","IMPRINT",FACE,{"disambiguationData":[TD([[makeQuery(id+"F4.imprint","IMPRINT",EDGE,{"disambiguationData":[TD([[subQ2,-1.0]])],"derivedFrom":subQ1}),-1.0]])]});}
            var Q11;
            {var subQ0=sQuery(id+"F4.wireOp",EDGE,"E113.trimOffspring");var subQ1=sQuery(id+"F4.wireOp",EDGE,"E93");var subQ2=makeQuery(id+"F4.imprint","INTERSECT",VERTEX,{"disambiguationData":[OD(0.0)],"derivedFrom":[subQ1,subQ0]});Q11=makeQuery(id+"F4.imprint","IMPRINT",FACE,{"disambiguationData":[TD([[makeQuery(id+"F4.imprint","IMPRINT",EDGE,{"disambiguationData":[TD([[subQ2,1.0]])],"derivedFrom":subQ1}),-1.0]])]});}
            var Q12;
            {var subQ0=sQuery(id+"F4.wireOp",EDGE,"E113.trimOffspring");var subQ1=sQuery(id+"F4.wireOp",EDGE,"E93");var subQ2=makeQuery(id+"F4.imprint","INTERSECT",VERTEX,{"disambiguationData":[OD(1.0)],"derivedFrom":[subQ1,subQ0]});Q12=makeQuery(id+"F4.imprint","IMPRINT",FACE,{"disambiguationData":[TD([[makeQuery(id+"F4.imprint","IMPRINT",EDGE,{"disambiguationData":[TD([[subQ2,-1.0]])],"derivedFrom":subQ1}),-1.0]])]});}
            var Q13;
            Q13=makeQuery(id+"F2.imprint","IMPRINT",FACE,{"disambiguationData":[TD([[makeQuery(id+"F2.imprint","IMPRINT",EDGE,{"derivedFrom":sQuery(id+"F2.wireOp",EDGE,"E79.bottom")}),-1.0]])]});
            var Q14;
            Q14=makeQuery(id+"F2.imprint","IMPRINT",FACE,{"disambiguationData":[TD([[makeQuery(id+"F2.imprint","IMPRINT",EDGE,{"derivedFrom":sQuery(id+"F2.wireOp",EDGE,"E79.bottom")}),1.0]])]});
            var Q15;
            Q15=makeQuery(id+"F0.imprint","IMPRINT",FACE,{"disambiguationData":[TD([[makeQuery(id+"F0.imprint","IMPRINT",EDGE,{"derivedFrom":sQuery(id+"F0.wireOp",EDGE,"E5.left")}),1.0]])]});
            var Q16;
            {var subQ0=sQuery(id+"F0.wireOp",EDGE,"E14.top");var subQ1=sQuery(id+"F0.wireOp",EDGE,"E1");var subQ2=makeQuery(id+"F0.imprint","INTERSECT",VERTEX,{"disambiguationData":[OD(0.0)],"derivedFrom":[subQ1,subQ0]});Q16=makeQuery(id+"F0.imprint","IMPRINT",FACE,{"disambiguationData":[TD([[makeQuery(id+"F0.imprint","IMPRINT",EDGE,{"disambiguationData":[TD([[subQ2,-1.0]])],"derivedFrom":subQ1}),1.0]])]});}
            var Q17;
            {var subQ0=sQuery(id+"F0.wireOp",EDGE,"E14.left");var subQ1=sQuery(id+"F0.wireOp",EDGE,"E1");var subQ2=makeQuery(id+"F0.imprint","INTERSECT",VERTEX,{"disambiguationData":[OD(0.0)],"derivedFrom":[subQ1,subQ0]});Q17=makeQuery(id+"F0.imprint","IMPRINT",FACE,{"disambiguationData":[TD([[makeQuery(id+"F0.imprint","IMPRINT",EDGE,{"disambiguationData":[TD([[subQ2,-1.0]])],"derivedFrom":subQ1}),1.0]])]});}
            var Q18;
            {var subQ0=sQuery(id+"F0.wireOp",EDGE,"E14.bottom");var subQ1=sQuery(id+"F0.wireOp",EDGE,"E1");var subQ2=makeQuery(id+"F0.imprint","INTERSECT",VERTEX,{"disambiguationData":[OD(0.0)],"derivedFrom":[subQ1,subQ0]});Q18=makeQuery(id+"F0.imprint","IMPRINT",FACE,{"disambiguationData":[TD([[makeQuery(id+"F0.imprint","IMPRINT",EDGE,{"disambiguationData":[TD([[subQ2,-1.0]])],"derivedFrom":subQ1}),1.0]])]});}
            var Q19;
            Q19=makeQuery(id+"F0.imprint","IMPRINT",FACE,{"disambiguationData":[TD([[makeQuery(id+"F0.imprint","IMPRINT",EDGE,{"derivedFrom":sQuery(id+"F0.wireOp",EDGE,"E5.bottom")}),1.0]])]});
            var Q20;
            Q20=makeQuery(id+"F0.imprint","IMPRINT",FACE,{"disambiguationData":[TD([[makeQuery(id+"F0.imprint","IMPRINT",EDGE,{"derivedFrom":sQuery(id+"F0.wireOp",EDGE,"E5.top")}),1.0]])]});
            var Q21;
            {var subQ0=sQuery(id+"F0.wireOp",EDGE,"E14.right");var subQ1=sQuery(id+"F0.wireOp",EDGE,"E1");var subQ2=makeQuery(id+"F0.imprint","INTERSECT",VERTEX,{"disambiguationData":[OD(0.0)],"derivedFrom":[subQ1,subQ0]});Q21=makeQuery(id+"F0.imprint","IMPRINT",FACE,{"disambiguationData":[TD([[makeQuery(id+"F0.imprint","IMPRINT",EDGE,{"disambiguationData":[TD([[subQ2,1.0]])],"derivedFrom":subQ1}),1.0]])]});}
            var Q22;
            Q22=makeQuery(id+"F0.imprint","IMPRINT",FACE,{"disambiguationData":[TD([[makeQuery(id+"F0.imprint","IMPRINT",EDGE,{"derivedFrom":sQuery(id+"F0.wireOp",EDGE,"E5.bottom")}),-1.0]])]});
            var Q23;
            {var subQ0=sQuery(id+"F1.wireOp",EDGE,"E35");var subQ1=makeQuery(id+"F1.imprint","INTERSECT",VERTEX,{"derivedFrom":[subQ0,sQuery(id+"F1.wireOp",EDGE,"E36.top")]});Q23=makeQuery(id+"F1.imprint","IMPRINT",FACE,{"disambiguationData":[TD([[makeQuery(id+"F1.imprint","IMPRINT",EDGE,{"disambiguationData":[TD([[subQ1,1.0]])],"derivedFrom":subQ0}),1.0]])]});}
            var Q24;
            Q24=makeQuery(id+"F1.imprint","IMPRINT",FACE,{"disambiguationData":[TD([[makeQuery(id+"F1.imprint","IMPRINT",EDGE,{"derivedFrom":sQuery(id+"F1.wireOp",EDGE,"E48.MirrorC")}),-1.0]])]});
            var Q25;
            Q25=makeQuery(id+"F1.imprint","IMPRINT",FACE,{"disambiguationData":[TD([[makeQuery(id+"F1.imprint","IMPRINT",EDGE,{"derivedFrom":sQuery(id+"F1.wireOp",EDGE,"E47")}),1.0]])]});
            var Q26;
            Q26=makeQuery(id+"F1.imprint","IMPRINT",FACE,{"disambiguationData":[TD([[makeQuery(id+"F1.imprint","IMPRINT",EDGE,{"derivedFrom":sQuery(id+"F1.wireOp",EDGE,"E49.bottom")}),-1.0]])]});
            var Q27;
            Q27=makeQuery(id+"F6.opExtrude","CAP_FACE",FACE,{"disambiguationData":[OSD([sQuery(id+"F3.wireOp",EDGE,"E86.bottom"),sQuery(id+"F3.wireOp",EDGE,"E86.top"),sQuery(id+"F3.wireOp",EDGE,"E86.left"),sQuery(id+"F3.wireOp",EDGE,"E86.right"),sQuery(id+"F3.wireOp",EDGE,"E87"),sQuery(id+"F3.wireOp",EDGE,"E88"),sQuery(id+"F3.wireOp",EDGE,"E89"),sQuery(id+"F3.wireOp",EDGE,"E90")])],"isStart":false});
            extrude(context, id + "F8", {"entities" : qUnion([Q0, Q1, Q2, Q3, Q4, Q5, Q6, Q7, Q8, Q9, Q10, Q11, Q12, Q13, Q14, Q15, Q16, Q17, Q18, Q19, Q20, Q21, Q22, Q23, Q24, Q25, Q26]), "operationType" : NewBodyOperationType.REMOVE, "endBound" : BoundingType.SYMMETRIC, "depth" : 3 * mm, "endBoundEntityFace" : qUnion([Q27]), "offsetDistance" : 25 * mm});
        }
        {
            var Q0;
            Q0=makeQuery(id+"F8.boolean.opBoolean","INTERSECT",EDGE,{"derivedFrom":[makeQuery(id+"F6.opExtrude","CAP_FACE",FACE,{"disambiguationData":[OSD([sQuery(id+"F3.wireOp",EDGE,"E86.bottom"),sQuery(id+"F3.wireOp",EDGE,"E86.top"),sQuery(id+"F3.wireOp",EDGE,"E86.left"),sQuery(id+"F3.wireOp",EDGE,"E86.right"),sQuery(id+"F3.wireOp",EDGE,"E87"),sQuery(id+"F3.wireOp",EDGE,"E88"),sQuery(id+"F3.wireOp",EDGE,"E89"),sQuery(id+"F3.wireOp",EDGE,"E90")])],"isStart":false}),makeQuery(id+"F8.opExtrude","SWEPT_FACE",FACE,{"disambiguationData":[OSD([sQuery(id+"F2.wireOp",EDGE,"E80")])]})]});
            chamfer(context, id + "F9", {"entities" : qUnion([Q0]), "width" : 4 * mm, "tangentPropagation" : true});
        }
        {
            var Q0;
            Q0=makeQuery(id+"F7.opExtrude","CAP_EDGE",EDGE,{"disambiguationData":[OSD([sQuery(id+"F1.wireOp",EDGE,"E47")])],"isStart":false});
            var Q1;
            Q1=makeQuery(id+"F7.opExtrude","CAP_EDGE",EDGE,{"disambiguationData":[OSD([sQuery(id+"F1.wireOp",EDGE,"E48.MirrorC")])],"isStart":false});
            chamfer(context, id + "F10", {"entities" : qUnion([Q0, Q1]), "width" : 1.5 * mm, "tangentPropagation" : true});
        }
        {
            var Q0;
            Q0=makeQuery(id+"F7.opExtrude","CAP_EDGE",EDGE,{"disambiguationData":[OSD([sQuery(id+"F2.wireOp",EDGE,"E81")])],"isStart":false});
            chamfer(context, id + "F11", {"entities" : qUnion([Q0]), "width" : 1.5 * mm, "tangentPropagation" : true});
        }
        {
            var Q0;
            Q0=makeQuery(id+"F7.opExtrude","CAP_FACE",FACE,{"disambiguationData":[OSD([sQuery(id+"F4.wireOp",EDGE,"E97.bottom"),sQuery(id+"F4.wireOp",EDGE,"E97.top"),sQuery(id+"F4.wireOp",EDGE,"E97.left"),sQuery(id+"F4.wireOp",EDGE,"E97.right"),sQuery(id+"F4.wireOp",EDGE,"E121"),sQuery(id+"F4.wireOp",EDGE,"E122"),sQuery(id+"F4.wireOp",EDGE,"E127.0"),sQuery(id+"F4.wireOp",EDGE,"E127.1"),sQuery(id+"F4.wireOp",EDGE,"E127.2"),sQuery(id+"F4.wireOp",EDGE,"E127.3")])],"isStart":false});
            var sketch = newSketch(context, id + "F12", { "sketchPlane" : qUnion([Q0])});
            skLineSegment(sketch, "E154", {"start": v(-41.9, 1.5) * mm, "end": v(-48.9, 1.5) * mm});
            skLineSegment(sketch, "E155", {"start": v(-48.9, 1.5) * mm, "end": v(-48.9, 2) * mm});
            skPoint(sketch, "E155.endSnap0", {"position": v(-48.9, 2) * mm});
            skLineSegment(sketch, "E156", {"start": v(-48.9, 2) * mm, "end": v(-42.4, 2) * mm});
            skLineSegment(sketch, "E157", {"start": v(-42.4, 2) * mm, "end": v(-42.4, 8.5) * mm});
            skLineSegment(sketch, "E158", {"start": v(-42.4, 8.5) * mm, "end": v(-41.9, 8.5) * mm});
            skLineSegment(sketch, "E159", {"start": v(-41.9, 8.5) * mm, "end": v(-41.9, 1.5) * mm});
            skSolve(sketch);
        }
        {
            var Q0;
            Q0=makeQuery(id+"F12.imprint","IMPRINT",FACE,{"disambiguationData":[TD([[makeQuery(id+"F12.imprint","IMPRINT",EDGE,{"derivedFrom":sQuery(id+"F12.wireOp",EDGE,"E154")}),1.0]])]});
            extrude(context, id + "F13", {"entities" : qUnion([Q0]), "depth" : 1 * mm, "offsetDistance" : 25 * mm});
        }
    });
